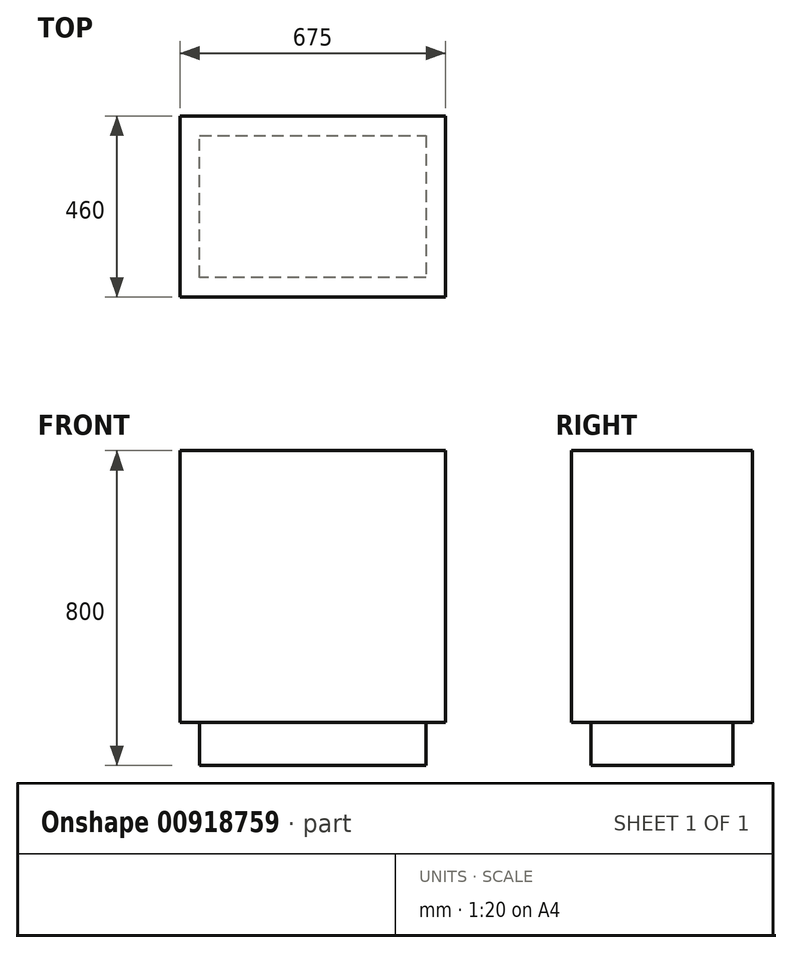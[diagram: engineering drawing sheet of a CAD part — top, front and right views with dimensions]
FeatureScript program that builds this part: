
annotation { "Feature Type Name" : "Feature", "Feature Type Description" : "" }
export const myFeature = defineFeature(function(context is Context, id is Id, definition is map)
    precondition{}
    {
        {
            var Q0;
            Q0=qCreatedBy(makeId("Top.planeOp"),FACE);
            cPlane(context, id + "F0", {"entities" : qUnion([Q0]), "cplaneType" : CPlaneType.OFFSET, "offset" : 800 * mm, "width" : 150 * mm, "height" : 150 * mm});
        }
        {
            var Q0;
            Q0=qCreatedBy(id+"F0.planeOp",FACE);
            var sketch = newSketch(context, id + "F1", { "sketchPlane" : qUnion([Q0])});
            skLineSegment(sketch, "E0.bottom", {"start": v(0, 0) * mm, "end": v(675, 0) * mm});
            skLineSegment(sketch, "E0.top", {"start": v(0, 460) * mm, "end": v(675, 460) * mm});
            skLineSegment(sketch, "E0.left", {"start": v(0, 0) * mm, "end": v(0, 460) * mm});
            skLineSegment(sketch, "E0.right", {"start": v(675, 0) * mm, "end": v(675, 460) * mm});
            skSolve(sketch);
        }
        {
            var Q0;
            Q0 = qSketchRegion(id + "F1", true);
            var Q1;
            Q1=qCreatedBy(makeId("Top.planeOp"),FACE);
            extrude(context, id + "F2", {"entities" : qUnion([Q0]), "endBound" : BoundingType.UP_TO_SURFACE, "oppositeDirection" : true, "depth" : 755 * mm, "endBoundEntityFace" : qUnion([Q1]), "hasOffset" : true, "offsetDistance" : 110 * mm});
        }
        {
            var Q0;
            Q0=makeQuery(id+"F2.opExtrude","CAP_FACE",FACE,{"disambiguationData":[OSD([sQuery(id+"F1.wireOp",EDGE,"E0.bottom"),sQuery(id+"F1.wireOp",EDGE,"E0.top"),sQuery(id+"F1.wireOp",EDGE,"E0.left"),sQuery(id+"F1.wireOp",EDGE,"E0.right")])],"isStart":false});
            var sketch = newSketch(context, id + "F3", { "sketchPlane" : qUnion([Q0])});
            skLineSegment(sketch, "E1.0", {"start": v(625, -410) * mm, "end": v(625, -50) * mm});
            skLineSegment(sketch, "E1.1", {"start": v(50, -410) * mm, "end": v(625, -410) * mm});
            skLineSegment(sketch, "E1.2", {"start": v(50, -50) * mm, "end": v(50, -410) * mm});
            skLineSegment(sketch, "E1.3", {"start": v(625, -50) * mm, "end": v(50, -50) * mm});
            skSolve(sketch);
        }
        {
            var Q0;
            Q0 = qSketchRegion(id + "F3", true);
            var Q1;
            Q1=qCreatedBy(makeId("Top.planeOp"),FACE);
            extrude(context, id + "F4", {"entities" : qUnion([Q0]), "operationType" : NewBodyOperationType.ADD, "endBound" : BoundingType.UP_TO_SURFACE, "depth" : 25 * mm, "endBoundEntityFace" : qUnion([Q1]), "offsetDistance" : 25 * mm});
        }
    });
